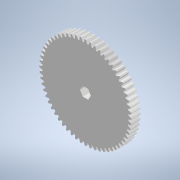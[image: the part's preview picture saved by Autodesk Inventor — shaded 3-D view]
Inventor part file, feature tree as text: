
AUTODESK INVENTOR PART (.ipt)
format: ipt  version: 2022 (Build 260153000, 153)  size: 3,827,200 bytes
history: native  units: mm
features: sketch x2, extrude x2
ambient origin geometry x8: Origin, YZ Plane, XZ Plane, XY Plane, X Axis, Y Axis, Z Axis, Center Point
bodies: Solid1 (feature_tree)
feature tree (4):
  sketch  "Sketch1"  dims[d0=6.2mm d1=0.0mm d20=3.1mm]
  extrude  "Extrusion1"  Depth=6.2mm
  extrude  "Extrusion7"  Depth=0.5mm
  sketch  "Sketch4"  dims[d21=60.0mm d23=360.0deg d34=0.5mm d35=10.0mm d36=0.0mm]
